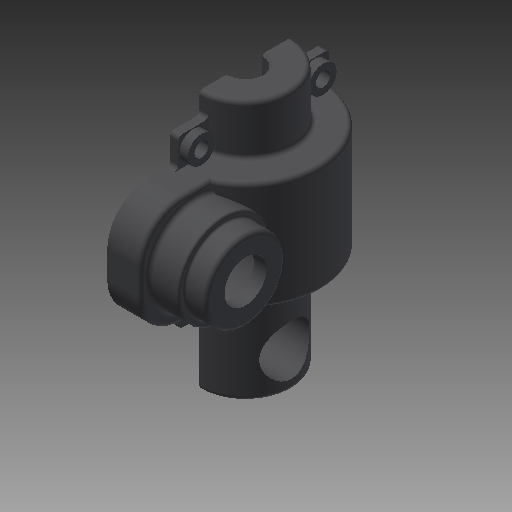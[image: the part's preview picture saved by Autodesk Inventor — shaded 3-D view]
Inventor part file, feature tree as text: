
AUTODESK INVENTOR PART (.ipt)
format: ipt  version: 2019 (Build 230136000, 136)  size: 477,184 bytes
history: native  units: mm
features: extrude x10, fillet x6, sketch x5, projected_geometry x2, plane x1, revolve x1, split x1, hole x1, chamfer x1, mirror x1
ambient origin geometry x8: Origin, YZ Plane, XZ Plane, XY Plane, X Axis, Y Axis, Z Axis, Center Point
bodies: Solid1 (feature_tree)
feature tree (29):
  extrude  "Extrusion1"  Depth=62.0mm TaperAngle=0.0deg
  plane  "Work Plane1"
  extrude  "Extrusion2"  Depth=36.0mm
  sketch  "Sketch3"  dims[d5=26.0mm d6=0.0mm d7=22.0mm]
  extrude  "Extrusion3"  Depth=22.0mm
  extrude  "Extrusion4"  Depth=15.0mm
  extrude  "Extrusion5"  Depth=16.0mm TaperAngle=0.0deg
  extrude  "Extrusion6"  Depth=1.0mm TaperAngle=0.0deg
  revolve  "Revolution1"  [1 undecoded]
  split  "Split1"
  extrude  "Extrusion7"  Depth=1.0mm
  extrude  "Extrusion8"  Depth=1.0mm TaperAngle=0.0deg
  fillet  "Fillet7"  Radius=34.0mm
  fillet  "Fillet8"  Radius=9.05mm
  fillet  "Fillet9"  Radius=9.0mm
  sketch  "Sketch5"  dims[d10=13.0mm d11=16.0mm d12=0.0mm d13=30.0mm d14=0.0mm d15=19.0mm d16=17.0mm d17=40.0mm d18=0.0mm d19=34.0mm d20=0.0mm d25=9.05mm d26=9.0mm d28=6.0mm d29=4.05mm d30=2.0mm d31=14.65mm d32=90.0deg d34=12.0mm d35=8.374731mm d36=56.0mm d37=0.0mm d40=10.0mm d41=56.0mm d42=0.0mm d47=10.0mm d48=1.0mm d49=0.5mm d51=7.0mm d52=7.0mm d53=3.5mm d54=3.5mm d56=2.0mm d57=0.0mm d67=26.0mm d78=6.5mm d79=6.5mm d80=6.5mm d81=6.5mm d82=4.0mm d83=0.0mm d84=3.4mm d85=6.0mm d86=6.3mm d87=2.0mm d88=90.0deg d89=4.0mm d90=20.594885mm d91=2.0mm d92=0.5mm d93=2.0mm d94=45.0deg d95=1.0mm d96=1.0mm d97=1.0mm d99=0.625269mm]
  extrude  "Extrusion9"  Depth=1.0mm
  extrude  "Extrusion11"  Depth=1.0mm
  hole  "Hole2"  [1 undecoded]
  chamfer  "Chamfer1"  Distance=14.65mm
  fillet  "Fillet13"  [1 undecoded]
  fillet  "Fillet14"  Radius=12.0mm
  fillet  "Fillet15"  Radius=8.374731mm
  mirror  "Mirror1"
  sketch  "Sketch1"  dims[d0=22.0mm d1=62.0mm d2=0.0mm]
  sketch  "Sketch2"  dims[d3=-24.0mm d4=36.0mm]
  sketch  "Sketch4"  dims[d8=20.0mm d9=15.0mm]
  projected_geometry  "Project Cut Edges1"
  projected_geometry  "Project Cut Edges2"
note: 3 required parameter values undecoded (feature->parameter linkage not recoverable at this tier; creation-order binding heuristic only, values carry confidence <= 0.55)